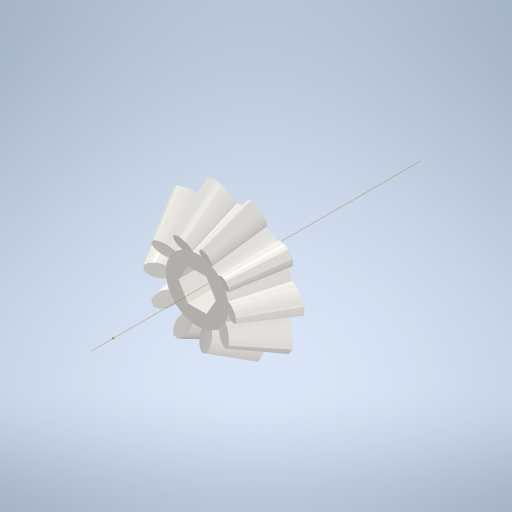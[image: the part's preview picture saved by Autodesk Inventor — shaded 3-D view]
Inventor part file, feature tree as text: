
AUTODESK INVENTOR PART (.ipt)
format: ipt  version: 2024.3 (Build 283343000, 343)  size: 569,344 bytes
history: native  units: mm
features: other x27, loft x2, pattern_circular x2, extrude x1, sketch x1, reference x1
ambient origin geometry x6: Origin, XZ Plane, X Axis, Y Axis, Z Axis, Center Point
bodies: Solid1 (feature_tree)
feature tree (34):
  other  "Top Point"
  other  "Mesh Plane2"
  other  "Teeth Body"
  other  "Start Point"
  other  "Tooth Plane"
  other  "Start Sketch"
  other  "End Point"
  other  "3D Sketch Right"
  other  "End Plane Right"
  loft  "Loft Right"
  pattern_circular  "Circular Pattern Right"  [2 undecoded]
  other  "3D Sketch Left"
  other  "End Plane Left"
  loft  "Loft Left"
  pattern_circular  "Circular Pattern Left"  [2 undecoded]
  other  "Fix Body"
  extrude  "Extrusion1"  TaperAngle=90.0deg  [1 undecoded]
  other  "Mesh Plane"
  other  "Top Plane"
  other  "Teeth Body Sketch"
  other  "End Plane"
  other  "End Sketch"
  other  "Helical Curve Left"
  other  "End Sketch Left"
  other  "Body Sketch"
  other  "Srf1"
  other  "Helical Curve Right"
  other  "End Sketch Right"
  sketch  "Sketch8"  dims[d0=10.0mm d1=7.853375mm d2=11.580644mm d3=4.0mm d4=9.604839mm d5=90.0deg d7=2.054002mm d8=2.596628mm d9=4.55392mm d11=4.10418mm d12=1.3mm d15=1.643434mm d16=2.882226mm d17=0.0mm d18=90.0deg d19=0.0mm d20=90.0deg d21=100.0mm d22=360.0deg d26=63.391752mm d27=3.67089mm d28=10.0mm d29=-4.636476mm d30=1.3mm d31=1.643434mm d32=2.882226mm d35=0.0mm d37=0.0mm d39=0.0mm d40=90.0deg d41=100.0mm d42=360.0deg d46=90.0deg d47=90.0deg d48=0.0mm d49=0.0mm d50=90.0deg d51=3.141593mm d52=0.0mm d53=0.0mm d54=0.0mm d56=3.326736mm d57=7.098859mm d58=4.140137mm d59=4.492945mm d60=2.620338mm d61=4.492945mm d62=2.620338mm d65=63.391752mm d66=31.5mm d67=10.0mm d68=-4.636476mm d69=3.67089mm d70=1.643434mm d71=2.882226mm d72=1.3mm d73=2.620338mm d74=4.492945mm d75=0.0mm d77=0.0mm d79=0.0mm d80=90.0deg d81=100.0mm d82=360.0deg d84=10.0mm d85=20.0mm d86=20.0mm d87=10.0mm d88=0.0mm d89=0.0mm d90=90.0deg d91=90.0deg d92=90.0deg d93=90.0deg d94=0.2mm d95=0.0mm d96=0.0mm]
  reference  "Reference1"
  other  "Pitch Diameter"
  other  "<userpath> TUF\Documents\Inventor\ParkinsonDetection\ReductorTrimmer.iam"
  other  "ReductorTrimmer.iam"
  other  "3296W:1"
note: 5 required parameter values undecoded (feature->parameter linkage not recoverable at this tier; creation-order binding heuristic only, values carry confidence <= 0.55)
